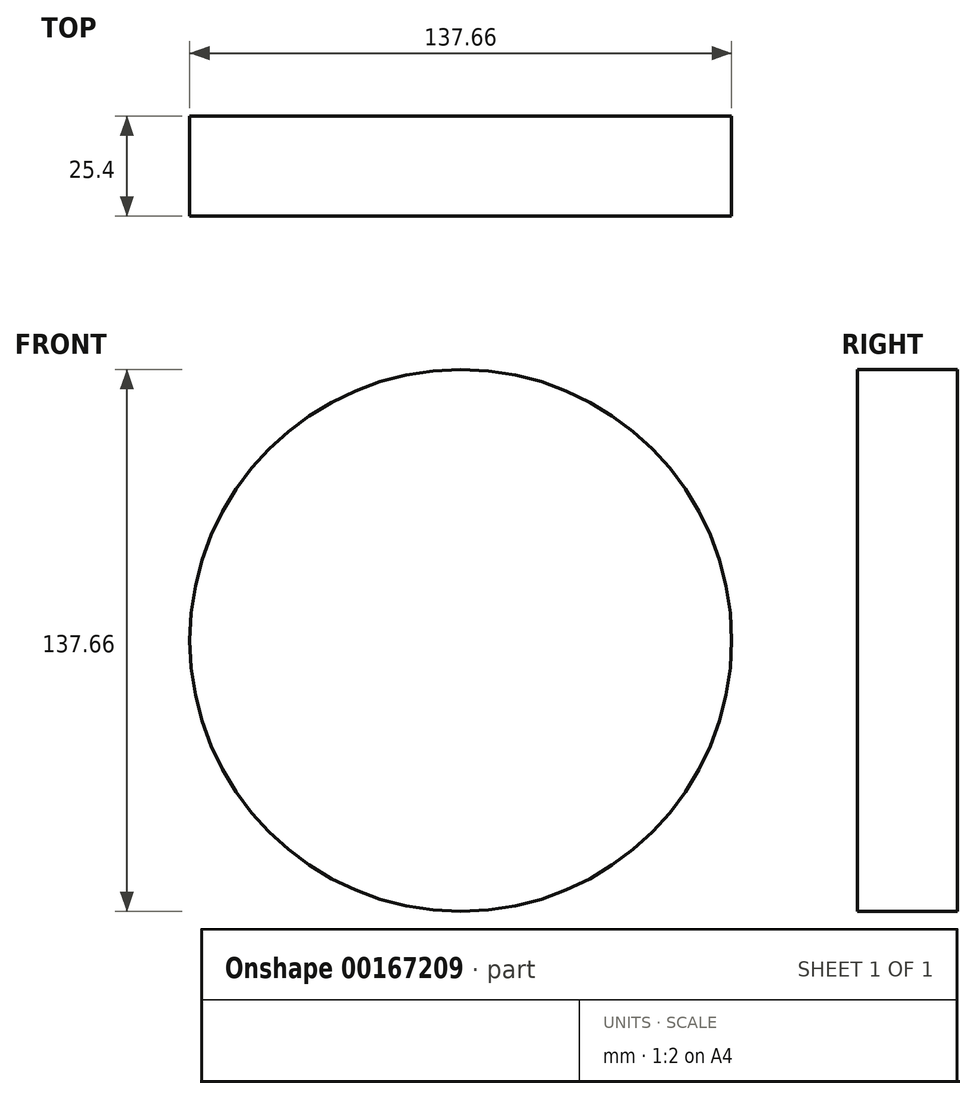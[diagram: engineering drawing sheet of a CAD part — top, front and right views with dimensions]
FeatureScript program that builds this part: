
annotation { "Feature Type Name" : "Feature", "Feature Type Description" : "" }
export const myFeature = defineFeature(function(context is Context, id is Id, definition is map)
    precondition{}
    {
        {
            var Q0;
            Q0=qCreatedBy(makeId("Front.planeOp"),FACE);
            var sketch = newSketch(context, id + "F0", { "sketchPlane" : qUnion([Q0])});
            skCircle(sketch, "E0", {"center": v(0, 0) * mm, "radius": 68.83 * mm});
            skSolve(sketch);
        }
        {
            var Q0;
            Q0=makeQuery(id+"F0.imprint","IMPRINT",FACE,{"disambiguationData":[TD([[makeQuery(id+"F0.imprint","IMPRINT",EDGE,{"derivedFrom":sQuery(id+"F0.wireOp",EDGE,"E0")}),1.0]])]});
            extrude(context, id + "F1", {"entities" : qUnion([Q0]), "depth" : 25.4 * mm});
        }
    });
